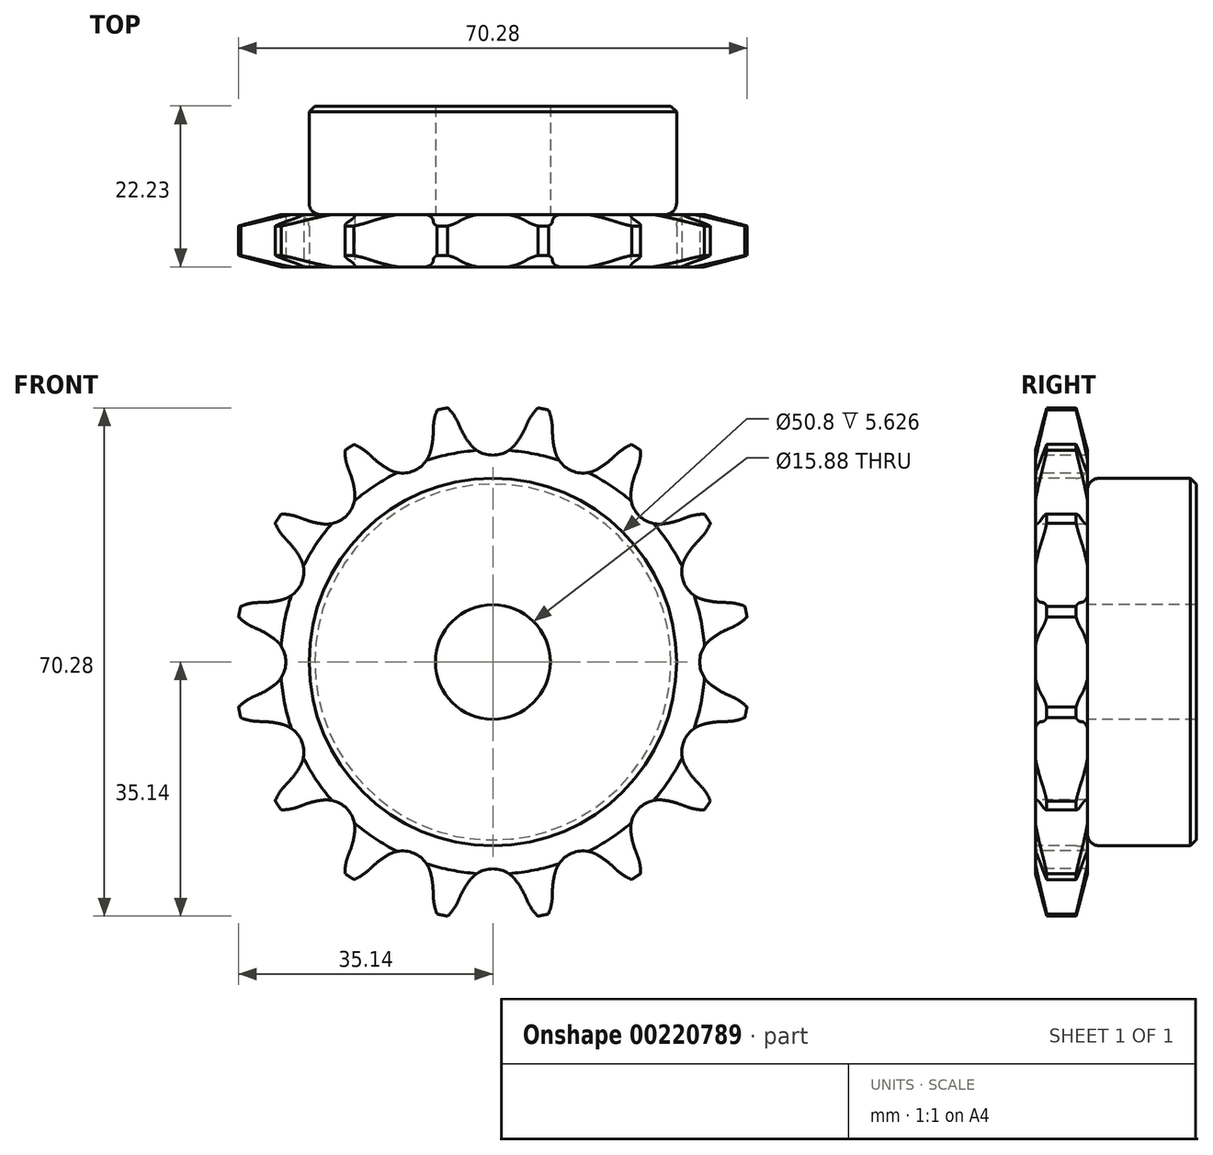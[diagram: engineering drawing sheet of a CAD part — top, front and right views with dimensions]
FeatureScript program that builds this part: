
annotation { "Feature Type Name" : "Feature", "Feature Type Description" : "" }
export const myFeature = defineFeature(function(context is Context, id is Id, definition is map)
    precondition{}
    {
        {
            var Q0;
            Q0=qCreatedBy(makeId("Right.planeOp"),FACE);
            var sketch = newSketch(context, id + "F0", { "sketchPlane" : qUnion([Q0])});
            skLineSegment(sketch, "E0", {"start": v(0, 0) * mm, "end": v(22.23, 0) * mm, "construction": true});
            skLineSegment(sketch, "E1.bottom", {"start": v(0, 7.94) * mm, "end": v(7.21, 7.94) * mm});
            skLineSegment(sketch, "E1.top", {"start": v(0, 35.69) * mm, "end": v(7.21, 35.69) * mm});
            skLineSegment(sketch, "E1.left", {"start": v(0, 7.94) * mm, "end": v(0, 35.69) * mm});
            skLineSegment(sketch, "E1.right", {"start": v(7.21, 7.94) * mm, "end": v(7.21, 35.69) * mm});
            skLineSegment(sketch, "E2.bottom", {"start": v(0, 7.94) * mm, "end": v(22.23, 7.94) * mm});
            skLineSegment(sketch, "E2.top", {"start": v(0, 25.4) * mm, "end": v(22.23, 25.4) * mm});
            skLineSegment(sketch, "E2.left", {"start": v(0, 7.94) * mm, "end": v(0, 25.4) * mm});
            skLineSegment(sketch, "E2.right", {"start": v(22.23, 7.94) * mm, "end": v(22.23, 25.4) * mm});
            skLineSegment(sketch, "E3.MirrorCS", {"start": v(0, -7.94) * mm, "end": v(7.21, -7.94) * mm});
            skLineSegment(sketch, "E4.MirrorCS", {"start": v(0, -25.4) * mm, "end": v(22.23, -25.4) * mm});
            skLineSegment(sketch, "E5.MirrorCS", {"start": v(0, -7.94) * mm, "end": v(22.23, -7.94) * mm});
            skLineSegment(sketch, "E6.MirrorCS", {"start": v(7.21, -7.94) * mm, "end": v(7.21, -35.69) * mm});
            skLineSegment(sketch, "E7.MirrorCS", {"start": v(0, -7.94) * mm, "end": v(0, -35.69) * mm});
            skLineSegment(sketch, "E8.MirrorCS", {"start": v(22.23, -7.94) * mm, "end": v(22.23, -25.4) * mm});
            skLineSegment(sketch, "E9.MirrorCS", {"start": v(0, -7.94) * mm, "end": v(0, -25.4) * mm});
            skLineSegment(sketch, "E10.MirrorCS", {"start": v(0, -35.69) * mm, "end": v(7.21, -35.69) * mm});
            skSolve(sketch);
        }
        {
            var Q0;
            {var subQ0=sQuery(id+"F0.wireOp",EDGE,"E1.top");Q0=makeQuery(id+"F0.imprint","IMPRINT",FACE,{"disambiguationData":[TD([[makeQuery(id+"F0.imprint","IMPRINT",EDGE,{"derivedFrom":subQ0}),-1.0]])]});}
            var Q1;
            {var subQ5=sQuery(id+"F0.wireOp",EDGE,"E2.left");Q1=makeQuery(id+"F0.imprint","IMPRINT",FACE,{"disambiguationData":[TD([[makeQuery(id+"F0.imprint","IMPRINT",EDGE,{"derivedFrom":subQ5}),-1.0]])]});}
            var Q2;
            {var subQ5=sQuery(id+"F0.wireOp",EDGE,"E2.right");Q2=makeQuery(id+"F0.imprint","IMPRINT",FACE,{"disambiguationData":[TD([[makeQuery(id+"F0.imprint","IMPRINT",EDGE,{"derivedFrom":subQ5}),1.0]])]});}
            var Q3;
            Q3=sQuery(id+"F0.wireOp",EDGE,"E0");
            revolve(context, id + "F1", {"entities" : qUnion([Q0, Q1, Q2]), "axis" : qUnion([Q3]), "revolveType" : RevolveType.FULL});
        }
        {
            var Q0;
            Q0=makeQuery(id+"F1.opRevolve","SWEPT_EDGE",EDGE,{"disambiguationData":[OSD([sQuery(id+"F0.wireOp",EDGE,"E1.right"),sQuery(id+"F0.wireOp",EDGE,"E2.top")])]});
            fillet(context, id + "F2", {"entities" : qUnion([Q0]), "radius" : 1.59 * mm, "tangentPropagation" : true, "allowEdgeOverflow" : false});
        }
        {
            var Q0;
            Q0=makeQuery(id+"F1.opRevolve","SWEPT_EDGE",EDGE,{"disambiguationData":[OSD([sQuery(id+"F0.wireOp",EDGE,"E2.top"),sQuery(id+"F0.wireOp",EDGE,"E2.right")])]});
            chamfer(context, id + "F3", {"entities" : qUnion([Q0]), "width" : 0.8 * mm, "tangentPropagation" : true});
        }
        {
            var Q0;
            Q0=makeQuery(id+"F1.opRevolve","SWEPT_EDGE",EDGE,{"disambiguationData":[OSD([sQuery(id+"F0.wireOp",EDGE,"E1.top"),sQuery(id+"F0.wireOp",EDGE,"E1.left")])]});
            var Q1;
            Q1=makeQuery(id+"F1.opRevolve","SWEPT_EDGE",EDGE,{"disambiguationData":[OSD([sQuery(id+"F0.wireOp",EDGE,"E1.top"),sQuery(id+"F0.wireOp",EDGE,"E1.right")])]});
            chamfer(context, id + "F4", {"entities" : qUnion([Q0, Q1]), "chamferType" : ChamferType.TWO_OFFSETS, "width1" : 6.35 * mm, "oppositeDirection" : false, "width2" : 1.57 * mm, "tangentPropagation" : true});
        }
        {
            var Q0;
            Q0=makeQuery(id+"F1.opRevolve","SWEPT_FACE",FACE,{"disambiguationData":[OSD([sQuery(id+"F0.wireOp",EDGE,"E1.left"),sQuery(id+"F0.wireOp",EDGE,"E2.left")])]});
            var sketch = newSketch(context, id + "F5", { "sketchPlane" : qUnion([Q0])});
            skArc(sketch, "E11", {"start": v(-4.8, 33.1) * mm, "mid": v(-5.78, 34.65) * mm, "end": v(-7.13, 35.87) * mm});
            skLineSegment(sketch, "E12", {"start": v(-4.45, 32.3) * mm, "end": v(-4.8, 33.1) * mm});
            skArc(sketch, "E13", {"start": v(-4.45, 32.3) * mm, "mid": v(-3.84, 31.15) * mm, "end": v(-3.1, 30.08) * mm});
            skArc(sketch, "E14", {"start": v(-3.1, 30.08) * mm, "mid": v(0.01, 28.6) * mm, "end": v(3.1, 30.1) * mm});
            skArc(sketch, "E15.MirrorCS", {"start": v(4.46, 32.32) * mm, "mid": v(3.85, 31.17) * mm, "end": v(3.1, 30.1) * mm});
            skLineSegment(sketch, "E16.MirrorCS", {"start": v(4.46, 32.32) * mm, "end": v(4.82, 33.12) * mm});
            skArc(sketch, "E17.MirrorCS", {"start": v(4.82, 33.12) * mm, "mid": v(5.79, 34.66) * mm, "end": v(7.14, 35.87) * mm});
            skLineSegment(sketch, "E18", {"start": v(0, 0) * mm, "end": v(0, 32.56) * mm, "construction": true});
            skArc(sketch, "E19.1.0", {"start": v(-17.1, 28.74) * mm, "mid": v(-18.6, 29.8) * mm, "end": v(-20.32, 30.41) * mm});
            skLineSegment(sketch, "E19.1.1", {"start": v(-16.47, 28.14) * mm, "end": v(-17.1, 28.74) * mm});
            skArc(sketch, "E19.1.2", {"start": v(-16.47, 28.14) * mm, "mid": v(-15.47, 27.3) * mm, "end": v(-14.37, 26.61) * mm});
            skArc(sketch, "E19.1.3", {"start": v(-14.37, 26.61) * mm, "mid": v(-10.93, 26.43) * mm, "end": v(-8.65, 29) * mm});
            skArc(sketch, "E19.1.4", {"start": v(-8.25, 31.57) * mm, "mid": v(-8.37, 30.27) * mm, "end": v(-8.65, 29) * mm});
            skLineSegment(sketch, "E19.1.5", {"start": v(-8.25, 31.57) * mm, "end": v(-8.22, 32.44) * mm});
            skArc(sketch, "E19.1.6", {"start": v(-8.22, 32.44) * mm, "mid": v(-7.91, 34.23) * mm, "end": v(-7.13, 35.87) * mm});
            skArc(sketch, "E19.2.0", {"start": v(-26.8, 20) * mm, "mid": v(-28.59, 20.42) * mm, "end": v(-30.4, 20.32) * mm});
            skLineSegment(sketch, "E19.2.1", {"start": v(-25.99, 19.7) * mm, "end": v(-26.8, 20) * mm});
            skArc(sketch, "E19.2.2", {"start": v(-25.99, 19.7) * mm, "mid": v(-24.74, 19.31) * mm, "end": v(-23.46, 19.09) * mm});
            skArc(sketch, "E19.2.3", {"start": v(-23.46, 19.09) * mm, "mid": v(-20.22, 20.23) * mm, "end": v(-19.09, 23.48) * mm});
            skArc(sketch, "E19.2.4", {"start": v(-19.7, 26.01) * mm, "mid": v(-19.31, 24.76) * mm, "end": v(-19.09, 23.48) * mm});
            skLineSegment(sketch, "E19.2.5", {"start": v(-19.7, 26.01) * mm, "end": v(-20, 26.83) * mm});
            skArc(sketch, "E19.2.6", {"start": v(-20, 26.83) * mm, "mid": v(-20.41, 28.6) * mm, "end": v(-20.32, 30.41) * mm});
            skArc(sketch, "E19.3.0", {"start": v(-32.42, 8.22) * mm, "mid": v(-34.22, 7.92) * mm, "end": v(-35.87, 7.14) * mm});
            skLineSegment(sketch, "E19.3.1", {"start": v(-31.55, 8.25) * mm, "end": v(-32.42, 8.22) * mm});
            skArc(sketch, "E19.3.2", {"start": v(-31.55, 8.25) * mm, "mid": v(-30.25, 8.37) * mm, "end": v(-28.98, 8.66) * mm});
            skArc(sketch, "E19.3.3", {"start": v(-28.98, 8.66) * mm, "mid": v(-26.42, 10.96) * mm, "end": v(-26.62, 14.39) * mm});
            skArc(sketch, "E19.3.4", {"start": v(-28.15, 16.5) * mm, "mid": v(-27.32, 15.49) * mm, "end": v(-26.62, 14.39) * mm});
            skLineSegment(sketch, "E19.3.5", {"start": v(-28.15, 16.5) * mm, "end": v(-28.75, 17.13) * mm});
            skArc(sketch, "E19.3.6", {"start": v(-28.75, 17.13) * mm, "mid": v(-29.8, 18.61) * mm, "end": v(-30.4, 20.32) * mm});
            skArc(sketch, "E19.4.0", {"start": v(-33.1, -4.8) * mm, "mid": v(-34.65, -5.78) * mm, "end": v(-35.87, -7.13) * mm});
            skLineSegment(sketch, "E19.4.1", {"start": v(-32.3, -4.45) * mm, "end": v(-33.1, -4.8) * mm});
            skArc(sketch, "E19.4.2", {"start": v(-32.3, -4.45) * mm, "mid": v(-31.15, -3.84) * mm, "end": v(-30.08, -3.1) * mm});
            skArc(sketch, "E19.4.3", {"start": v(-30.08, -3.1) * mm, "mid": v(-28.6, 0.01) * mm, "end": v(-30.1, 3.1) * mm});
            skArc(sketch, "E19.4.4", {"start": v(-32.32, 4.46) * mm, "mid": v(-31.17, 3.85) * mm, "end": v(-30.1, 3.1) * mm});
            skLineSegment(sketch, "E19.4.5", {"start": v(-32.32, 4.46) * mm, "end": v(-33.12, 4.82) * mm});
            skArc(sketch, "E19.4.6", {"start": v(-33.12, 4.82) * mm, "mid": v(-34.66, 5.79) * mm, "end": v(-35.87, 7.14) * mm});
            skArc(sketch, "E19.5.0", {"start": v(-28.74, -17.1) * mm, "mid": v(-29.8, -18.6) * mm, "end": v(-30.41, -20.32) * mm});
            skLineSegment(sketch, "E19.5.1", {"start": v(-28.14, -16.47) * mm, "end": v(-28.74, -17.1) * mm});
            skArc(sketch, "E19.5.2", {"start": v(-28.14, -16.47) * mm, "mid": v(-27.3, -15.47) * mm, "end": v(-26.61, -14.37) * mm});
            skArc(sketch, "E19.5.3", {"start": v(-26.61, -14.37) * mm, "mid": v(-26.43, -10.93) * mm, "end": v(-29, -8.65) * mm});
            skArc(sketch, "E19.5.4", {"start": v(-31.57, -8.25) * mm, "mid": v(-30.27, -8.37) * mm, "end": v(-29, -8.65) * mm});
            skLineSegment(sketch, "E19.5.5", {"start": v(-31.57, -8.25) * mm, "end": v(-32.44, -8.22) * mm});
            skArc(sketch, "E19.5.6", {"start": v(-32.44, -8.22) * mm, "mid": v(-34.23, -7.91) * mm, "end": v(-35.87, -7.13) * mm});
            skArc(sketch, "E19.6.0", {"start": v(-20, -26.8) * mm, "mid": v(-20.42, -28.59) * mm, "end": v(-20.32, -30.4) * mm});
            skLineSegment(sketch, "E19.6.1", {"start": v(-19.7, -25.99) * mm, "end": v(-20, -26.8) * mm});
            skArc(sketch, "E19.6.2", {"start": v(-19.7, -25.99) * mm, "mid": v(-19.31, -24.74) * mm, "end": v(-19.09, -23.46) * mm});
            skArc(sketch, "E19.6.3", {"start": v(-19.09, -23.46) * mm, "mid": v(-20.23, -20.22) * mm, "end": v(-23.48, -19.09) * mm});
            skArc(sketch, "E19.6.4", {"start": v(-26.01, -19.7) * mm, "mid": v(-24.76, -19.31) * mm, "end": v(-23.48, -19.09) * mm});
            skLineSegment(sketch, "E19.6.5", {"start": v(-26.01, -19.7) * mm, "end": v(-26.83, -20) * mm});
            skArc(sketch, "E19.6.6", {"start": v(-26.83, -20) * mm, "mid": v(-28.6, -20.41) * mm, "end": v(-30.41, -20.32) * mm});
            skArc(sketch, "E19.7.0", {"start": v(-8.22, -32.42) * mm, "mid": v(-7.92, -34.22) * mm, "end": v(-7.14, -35.87) * mm});
            skLineSegment(sketch, "E19.7.1", {"start": v(-8.25, -31.55) * mm, "end": v(-8.22, -32.42) * mm});
            skArc(sketch, "E19.7.2", {"start": v(-8.25, -31.55) * mm, "mid": v(-8.37, -30.25) * mm, "end": v(-8.66, -28.98) * mm});
            skArc(sketch, "E19.7.3", {"start": v(-8.66, -28.98) * mm, "mid": v(-10.96, -26.42) * mm, "end": v(-14.39, -26.62) * mm});
            skArc(sketch, "E19.7.4", {"start": v(-16.5, -28.15) * mm, "mid": v(-15.49, -27.32) * mm, "end": v(-14.39, -26.62) * mm});
            skLineSegment(sketch, "E19.7.5", {"start": v(-16.5, -28.15) * mm, "end": v(-17.13, -28.75) * mm});
            skArc(sketch, "E19.7.6", {"start": v(-17.13, -28.75) * mm, "mid": v(-18.61, -29.8) * mm, "end": v(-20.32, -30.4) * mm});
            skArc(sketch, "E19.8.0", {"start": v(4.8, -33.1) * mm, "mid": v(5.78, -34.65) * mm, "end": v(7.13, -35.87) * mm});
            skLineSegment(sketch, "E19.8.1", {"start": v(4.45, -32.3) * mm, "end": v(4.8, -33.1) * mm});
            skArc(sketch, "E19.8.2", {"start": v(4.45, -32.3) * mm, "mid": v(3.84, -31.15) * mm, "end": v(3.1, -30.08) * mm});
            skArc(sketch, "E19.8.3", {"start": v(3.1, -30.08) * mm, "mid": v(-0.01, -28.6) * mm, "end": v(-3.1, -30.1) * mm});
            skArc(sketch, "E19.8.4", {"start": v(-4.46, -32.32) * mm, "mid": v(-3.85, -31.17) * mm, "end": v(-3.1, -30.1) * mm});
            skLineSegment(sketch, "E19.8.5", {"start": v(-4.46, -32.32) * mm, "end": v(-4.82, -33.12) * mm});
            skArc(sketch, "E19.8.6", {"start": v(-4.82, -33.12) * mm, "mid": v(-5.79, -34.66) * mm, "end": v(-7.14, -35.87) * mm});
            skArc(sketch, "E19.9.0", {"start": v(17.1, -28.74) * mm, "mid": v(18.6, -29.8) * mm, "end": v(20.32, -30.41) * mm});
            skLineSegment(sketch, "E19.9.1", {"start": v(16.47, -28.14) * mm, "end": v(17.1, -28.74) * mm});
            skArc(sketch, "E19.9.2", {"start": v(16.47, -28.14) * mm, "mid": v(15.47, -27.3) * mm, "end": v(14.37, -26.61) * mm});
            skArc(sketch, "E19.9.3", {"start": v(14.37, -26.61) * mm, "mid": v(10.93, -26.43) * mm, "end": v(8.65, -29) * mm});
            skArc(sketch, "E19.9.4", {"start": v(8.25, -31.57) * mm, "mid": v(8.37, -30.27) * mm, "end": v(8.65, -29) * mm});
            skLineSegment(sketch, "E19.9.5", {"start": v(8.25, -31.57) * mm, "end": v(8.22, -32.44) * mm});
            skArc(sketch, "E19.9.6", {"start": v(8.22, -32.44) * mm, "mid": v(7.91, -34.23) * mm, "end": v(7.13, -35.87) * mm});
            skArc(sketch, "E19.10.0", {"start": v(26.8, -20) * mm, "mid": v(28.59, -20.42) * mm, "end": v(30.4, -20.32) * mm});
            skLineSegment(sketch, "E19.10.1", {"start": v(25.99, -19.7) * mm, "end": v(26.8, -20) * mm});
            skArc(sketch, "E19.10.2", {"start": v(25.99, -19.7) * mm, "mid": v(24.74, -19.31) * mm, "end": v(23.46, -19.09) * mm});
            skArc(sketch, "E19.10.3", {"start": v(23.46, -19.09) * mm, "mid": v(20.22, -20.23) * mm, "end": v(19.09, -23.48) * mm});
            skArc(sketch, "E19.10.4", {"start": v(19.7, -26.01) * mm, "mid": v(19.31, -24.76) * mm, "end": v(19.09, -23.48) * mm});
            skLineSegment(sketch, "E19.10.5", {"start": v(19.7, -26.01) * mm, "end": v(20, -26.83) * mm});
            skArc(sketch, "E19.10.6", {"start": v(20, -26.83) * mm, "mid": v(20.41, -28.6) * mm, "end": v(20.32, -30.41) * mm});
            skArc(sketch, "E19.11.0", {"start": v(32.42, -8.22) * mm, "mid": v(34.22, -7.92) * mm, "end": v(35.87, -7.14) * mm});
            skLineSegment(sketch, "E19.11.1", {"start": v(31.55, -8.25) * mm, "end": v(32.42, -8.22) * mm});
            skArc(sketch, "E19.11.2", {"start": v(31.55, -8.25) * mm, "mid": v(30.25, -8.37) * mm, "end": v(28.98, -8.66) * mm});
            skArc(sketch, "E19.11.3", {"start": v(28.98, -8.66) * mm, "mid": v(26.42, -10.96) * mm, "end": v(26.62, -14.39) * mm});
            skArc(sketch, "E19.11.4", {"start": v(28.15, -16.5) * mm, "mid": v(27.32, -15.49) * mm, "end": v(26.62, -14.39) * mm});
            skLineSegment(sketch, "E19.11.5", {"start": v(28.15, -16.5) * mm, "end": v(28.75, -17.13) * mm});
            skArc(sketch, "E19.11.6", {"start": v(28.75, -17.13) * mm, "mid": v(29.8, -18.61) * mm, "end": v(30.4, -20.32) * mm});
            skArc(sketch, "E19.12.0", {"start": v(33.1, 4.8) * mm, "mid": v(34.65, 5.78) * mm, "end": v(35.87, 7.13) * mm});
            skLineSegment(sketch, "E19.12.1", {"start": v(32.3, 4.45) * mm, "end": v(33.1, 4.8) * mm});
            skArc(sketch, "E19.12.2", {"start": v(32.3, 4.45) * mm, "mid": v(31.15, 3.84) * mm, "end": v(30.08, 3.1) * mm});
            skArc(sketch, "E19.12.3", {"start": v(30.08, 3.1) * mm, "mid": v(28.6, -0.01) * mm, "end": v(30.1, -3.1) * mm});
            skArc(sketch, "E19.12.4", {"start": v(32.32, -4.46) * mm, "mid": v(31.17, -3.85) * mm, "end": v(30.1, -3.1) * mm});
            skLineSegment(sketch, "E19.12.5", {"start": v(32.32, -4.46) * mm, "end": v(33.12, -4.82) * mm});
            skArc(sketch, "E19.12.6", {"start": v(33.12, -4.82) * mm, "mid": v(34.66, -5.79) * mm, "end": v(35.87, -7.14) * mm});
            skArc(sketch, "E19.13.0", {"start": v(28.74, 17.1) * mm, "mid": v(29.8, 18.6) * mm, "end": v(30.41, 20.32) * mm});
            skLineSegment(sketch, "E19.13.1", {"start": v(28.14, 16.47) * mm, "end": v(28.74, 17.1) * mm});
            skArc(sketch, "E19.13.2", {"start": v(28.14, 16.47) * mm, "mid": v(27.3, 15.47) * mm, "end": v(26.61, 14.37) * mm});
            skArc(sketch, "E19.13.3", {"start": v(26.61, 14.37) * mm, "mid": v(26.43, 10.93) * mm, "end": v(29, 8.65) * mm});
            skArc(sketch, "E19.13.4", {"start": v(31.57, 8.25) * mm, "mid": v(30.27, 8.37) * mm, "end": v(29, 8.65) * mm});
            skLineSegment(sketch, "E19.13.5", {"start": v(31.57, 8.25) * mm, "end": v(32.44, 8.22) * mm});
            skArc(sketch, "E19.13.6", {"start": v(32.44, 8.22) * mm, "mid": v(34.23, 7.91) * mm, "end": v(35.87, 7.13) * mm});
            skArc(sketch, "E19.14.0", {"start": v(20, 26.8) * mm, "mid": v(20.42, 28.59) * mm, "end": v(20.32, 30.4) * mm});
            skLineSegment(sketch, "E19.14.1", {"start": v(19.7, 25.99) * mm, "end": v(20, 26.8) * mm});
            skArc(sketch, "E19.14.2", {"start": v(19.7, 25.99) * mm, "mid": v(19.31, 24.74) * mm, "end": v(19.09, 23.46) * mm});
            skArc(sketch, "E19.14.3", {"start": v(19.09, 23.46) * mm, "mid": v(20.23, 20.22) * mm, "end": v(23.48, 19.09) * mm});
            skArc(sketch, "E19.14.4", {"start": v(26.01, 19.7) * mm, "mid": v(24.76, 19.31) * mm, "end": v(23.48, 19.09) * mm});
            skLineSegment(sketch, "E19.14.5", {"start": v(26.01, 19.7) * mm, "end": v(26.83, 20) * mm});
            skArc(sketch, "E19.14.6", {"start": v(26.83, 20) * mm, "mid": v(28.6, 20.41) * mm, "end": v(30.41, 20.32) * mm});
            skArc(sketch, "E19.15.0", {"start": v(8.22, 32.42) * mm, "mid": v(7.92, 34.22) * mm, "end": v(7.14, 35.87) * mm});
            skLineSegment(sketch, "E19.15.1", {"start": v(8.25, 31.55) * mm, "end": v(8.22, 32.42) * mm});
            skArc(sketch, "E19.15.2", {"start": v(8.25, 31.55) * mm, "mid": v(8.37, 30.25) * mm, "end": v(8.66, 28.98) * mm});
            skArc(sketch, "E19.15.3", {"start": v(8.66, 28.98) * mm, "mid": v(10.96, 26.42) * mm, "end": v(14.39, 26.62) * mm});
            skArc(sketch, "E19.15.4", {"start": v(16.5, 28.15) * mm, "mid": v(15.49, 27.32) * mm, "end": v(14.39, 26.62) * mm});
            skLineSegment(sketch, "E19.15.5", {"start": v(16.5, 28.15) * mm, "end": v(17.13, 28.75) * mm});
            skArc(sketch, "E19.15.6", {"start": v(17.13, 28.75) * mm, "mid": v(18.61, 29.8) * mm, "end": v(20.32, 30.4) * mm});
            skPoint(sketch, "E19.center", {"position": v(0, 0) * mm});
            skSolve(sketch);
        }
        {
            var Q0;
            Q0=qSketchRegion(id+"F5",true);
            extrude(context, id + "F6", {"entities" : qUnion([Q0]), "operationType" : NewBodyOperationType.INTERSECT, "endBound" : BoundingType.THROUGH_ALL, "oppositeDirection" : true, "depth" : 25.4 * mm});
        }
    });
